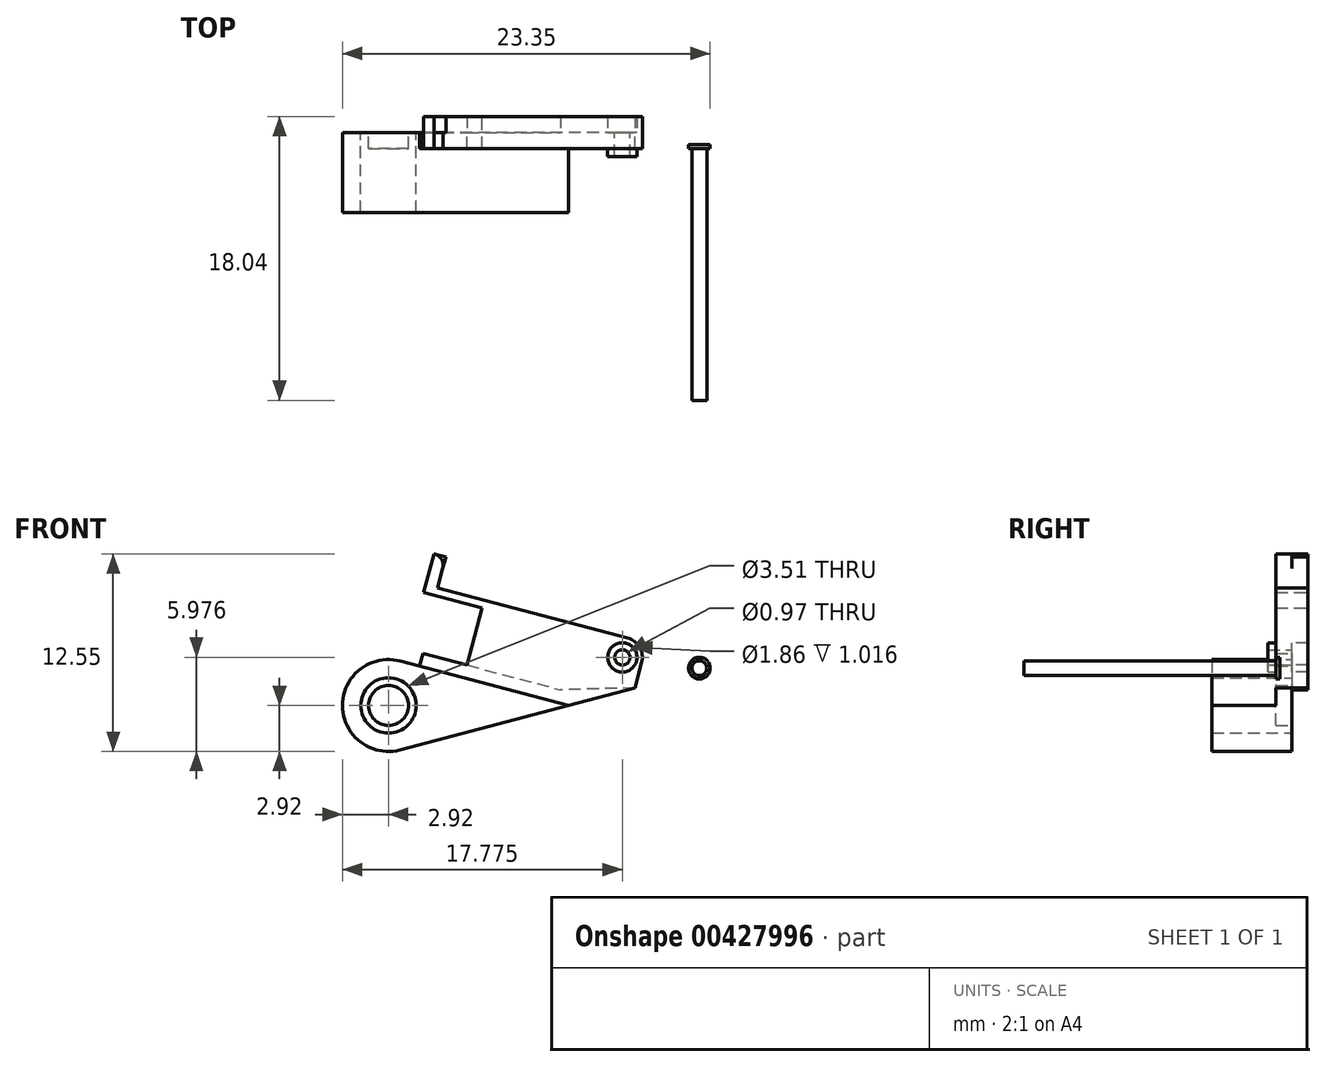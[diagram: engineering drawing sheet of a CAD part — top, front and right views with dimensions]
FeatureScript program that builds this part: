
annotation { "Feature Type Name" : "Feature", "Feature Type Description" : "" }
export const myFeature = defineFeature(function(context is Context, id is Id, definition is map)
    precondition{}
    {
        {
            var Q0;
            Q0=qCreatedBy(makeId("Front.planeOp"),FACE);
            var sketch = newSketch(context, id + "F0", { "sketchPlane" : qUnion([Q0])});
            skCircle(sketch, "E0", {"center": v(0, 0) * mm, "radius": 1.27 * mm});
            skCircle(sketch, "E1", {"center": v(0, 0) * mm, "radius": 2.92 * mm});
            skLineSegment(sketch, "E2", {"start": v(0.75, 2.82) * mm, "end": v(11.43, 0) * mm});
            skLineSegment(sketch, "E3", {"start": v(11.43, 0) * mm, "end": v(0.75, -2.82) * mm});
            skCircle(sketch, "E4", {"center": v(0, 0) * mm, "radius": 1.76 * mm});
            skLineSegment(sketch, "E5", {"start": v(1.97, 2.5) * mm, "end": v(2.19, 3.3) * mm});
            skLineSegment(sketch, "E6", {"start": v(2.19, 3.3) * mm, "end": v(4.98, 2.56) * mm});
            skLineSegment(sketch, "E7", {"start": v(4.98, 2.56) * mm, "end": v(5.94, 6.19) * mm});
            skLineSegment(sketch, "E8", {"start": v(5.94, 6.19) * mm, "end": v(2.24, 7.17) * mm});
            skLineSegment(sketch, "E9", {"start": v(2.24, 7.17) * mm, "end": v(2.89, 9.63) * mm});
            skLineSegment(sketch, "E10", {"start": v(2.89, 9.63) * mm, "end": v(3.64, 9.43) * mm});
            skLineSegment(sketch, "E11", {"start": v(3.64, 9.43) * mm, "end": v(3.13, 7.47) * mm});
            skLineSegment(sketch, "E12", {"start": v(3.13, 7.47) * mm, "end": v(9.67, 5.74) * mm});
            skLineSegment(sketch, "E13", {"start": v(9.67, 5.74) * mm, "end": v(15.18, 4.28) * mm});
            skLineSegment(sketch, "E14", {"start": v(16.08, 2.73) * mm, "end": v(15.66, 1.12) * mm});
            skLineSegment(sketch, "E15", {"start": v(15.66, 1.12) * mm, "end": v(11.43, 0) * mm});
            skPoint(sketch, "E16.visualSharp", {"position": v(16.4, 3.96) * mm});
            skArc(sketch, "E16.filletArc", {"start": v(16.08, 2.73) * mm, "mid": v(15.95, 3.7) * mm, "end": v(15.18, 4.28) * mm});
            skLineSegment(sketch, "E17", {"start": v(4.98, 2.56) * mm, "end": v(13.05, 0.43) * mm});
            skCircle(sketch, "E18", {"center": v(14.86, 3.06) * mm, "radius": 0.49 * mm});
            skCircle(sketch, "E19", {"center": v(14.86, 3.06) * mm, "radius": 0.93 * mm});
            skSolve(sketch);
        }
        {
            var Q0;
            Q0=makeQuery(id+"F0.imprint","IMPRINT",FACE,{"disambiguationData":[TD([[makeQuery(id+"F0.imprint","IMPRINT",EDGE,{"derivedFrom":sQuery(id+"F0.wireOp",EDGE,"E0")}),1.0]])]});
            var Q1;
            {var subQ0=sQuery(id+"F0.wireOp",EDGE,"E2");Q1=makeQuery(id+"F0.imprint","IMPRINT",FACE,{"disambiguationData":[TD([[makeQuery(id+"F0.imprint","IMPRINT",EDGE,{"derivedFrom":subQ0}),-1.0]])]});}
            var Q2;
            Q2=makeQuery(id+"F0.imprint","IMPRINT",FACE,{"disambiguationData":[TD([[makeQuery(id+"F0.imprint","IMPRINT",EDGE,{"derivedFrom":sQuery(id+"F0.wireOp",EDGE,"E4")}),-1.0]])]});
            extrude(context, id + "F1", {"entities" : qUnion([Q0, Q1, Q2]), "depth" : 5.08 * mm});
        }
        {
            var Q0;
            Q0=makeQuery(id+"F1.opExtrude","CAP_FACE",FACE,{"disambiguationData":[OSD([sQuery(id+"F0.wireOp",EDGE,"E0"),sQuery(id+"F0.wireOp",EDGE,"E1"),sQuery(id+"F0.wireOp",EDGE,"E2"),sQuery(id+"F0.wireOp",EDGE,"E3")])],"isStart":false});
            var sketch = newSketch(context, id + "F2", { "sketchPlane" : qUnion([Q0])});
            skCircle(sketch, "E20.0", {"center": v(0, 0) * mm, "radius": 1.76 * mm});
            skSolve(sketch);
        }
        {
            var Q0;
            Q0=makeQuery(id+"F2.imprint","IMPRINT",FACE,{"disambiguationData":[TD([[makeQuery(id+"F2.imprint","IMPRINT",EDGE,{"derivedFrom":sQuery(id+"F2.wireOp",EDGE,"E20.0")}),1.0]])]});
            extrude(context, id + "F3", {"entities" : qUnion([Q0]), "operationType" : NewBodyOperationType.REMOVE, "oppositeDirection" : true, "depth" : 4.06 * mm});
        }
        {
            var Q0;
            {var subQ4=sQuery(id+"F0.wireOp",EDGE,"E5");Q0=makeQuery(id+"F0.imprint","IMPRINT",FACE,{"disambiguationData":[TD([[makeQuery(id+"F0.imprint","IMPRINT",EDGE,{"derivedFrom":subQ4}),-1.0]])]});}
            extrude(context, id + "F4", {"entities" : qUnion([Q0]), "operationType" : NewBodyOperationType.ADD, "depth" : 1.02 * mm});
        }
        {
            var Q0;
            Q0=makeQuery(id+"F0.imprint","IMPRINT",FACE,{"disambiguationData":[TD([[makeQuery(id+"F0.imprint","IMPRINT",EDGE,{"derivedFrom":sQuery(id+"F0.wireOp",EDGE,"E7")}),-1.0]])]});
            var Q1;
            Q1=makeQuery(id+"F0.imprint","IMPRINT",FACE,{"disambiguationData":[TD([[makeQuery(id+"F0.imprint","IMPRINT",EDGE,{"derivedFrom":sQuery(id+"F0.wireOp",EDGE,"E18")}),-1.0]])]});
            extrude(context, id + "F5", {"entities" : qUnion([Q0, Q1]), "operationType" : NewBodyOperationType.ADD, "depth" : 1.02 * mm});
        }
        {
            var Q0;
            Q0=makeQuery(id+"F5.opExtrude","SWEPT_EDGE",EDGE,{"disambiguationData":[OSD([sQuery(id+"F0.wireOp",EDGE,"E10"),sQuery(id+"F0.wireOp",EDGE,"E11")])]});
            fillet(context, id + "F6", {"entities" : qUnion([Q0]), "radius" : 0.76 * mm, "tangentPropagation" : true, "allowEdgeOverflow" : false});
        }
        {
            var Q0;
            {var subQ0=sQuery(id+"F0.wireOp",EDGE,"E17");var subQ1=sQuery(id+"F0.wireOp",EDGE,"E15");Q0=makeQuery(id+"F5.boolean.opBoolean","MERGE",FACE,{"derivedFrom":[makeQuery(id+"F4.opExtrude","CAP_FACE",FACE,{"disambiguationData":[OSD([sQuery(id+"F0.wireOp",EDGE,"E2"),sQuery(id+"F0.wireOp",EDGE,"E5"),sQuery(id+"F0.wireOp",EDGE,"E6"),subQ1,subQ0])],"isStart":false}),makeQuery(id+"F5.opExtrude","CAP_FACE",FACE,{"disambiguationData":[OSD([sQuery(id+"F0.wireOp",EDGE,"E7"),sQuery(id+"F0.wireOp",EDGE,"E8"),sQuery(id+"F0.wireOp",EDGE,"E9"),sQuery(id+"F0.wireOp",EDGE,"E10"),sQuery(id+"F0.wireOp",EDGE,"E11"),sQuery(id+"F0.wireOp",EDGE,"E12"),sQuery(id+"F0.wireOp",EDGE,"E13"),sQuery(id+"F0.wireOp",EDGE,"E14"),subQ1,sQuery(id+"F0.wireOp",EDGE,"E16.filletArc"),subQ0,sQuery(id+"F0.wireOp",EDGE,"E18")])],"isStart":false})]});}
            var sketch = newSketch(context, id + "F7", { "sketchPlane" : qUnion([Q0])});
            skCircle(sketch, "E21.0", {"center": v(14.86, 3.06) * mm, "radius": 0.93 * mm});
            skSolve(sketch);
        }
        {
            var Q0;
            Q0=makeQuery(id+"F7.imprint","IMPRINT",FACE,{"disambiguationData":[TD([[makeQuery(id+"F7.imprint","IMPRINT",EDGE,{"derivedFrom":sQuery(id+"F7.wireOp",EDGE,"E21.0")}),1.0]])]});
            extrude(context, id + "F8", {"entities" : qUnion([Q0]), "operationType" : NewBodyOperationType.ADD, "depth" : 0.5 * mm});
        }
        {
            var Q0;
            Q0=makeQuery(id+"F0.imprint","IMPRINT",FACE,{"disambiguationData":[TD([[makeQuery(id+"F0.imprint","IMPRINT",EDGE,{"derivedFrom":sQuery(id+"F0.wireOp",EDGE,"E7")}),-1.0]])]});
            var sketch = newSketch(context, id + "F9", { "sketchPlane" : qUnion([Q0])});
            skLineSegment(sketch, "E22.0.0", {"start": v(11.43, 0) * mm, "end": v(13.05, 0.43) * mm});
            skLineSegment(sketch, "E22.0.1", {"start": v(13.05, 0.43) * mm, "end": v(4.98, 2.56) * mm});
            skLineSegment(sketch, "E22.0.2", {"start": v(4.98, 2.56) * mm, "end": v(2.19, 3.3) * mm});
            skLineSegment(sketch, "E22.0.3", {"start": v(2.19, 3.3) * mm, "end": v(1.97, 2.5) * mm});
            skLineSegment(sketch, "E22.0.4", {"start": v(1.97, 2.5) * mm, "end": v(11.43, 0) * mm});
            skLineSegment(sketch, "E23.0.0", {"start": v(5.94, 6.19) * mm, "end": v(4.98, 2.56) * mm});
            skLineSegment(sketch, "E23.0.1", {"start": v(4.98, 2.56) * mm, "end": v(13.05, 0.43) * mm});
            skLineSegment(sketch, "E23.0.2", {"start": v(13.05, 0.43) * mm, "end": v(15.66, 1.12) * mm});
            skLineSegment(sketch, "E23.0.3", {"start": v(15.66, 1.12) * mm, "end": v(16.08, 2.73) * mm});
            skArc(sketch, "E23.0.4", {"start": v(16.08, 2.73) * mm, "mid": v(15.95, 3.7) * mm, "end": v(15.18, 4.28) * mm});
            skLineSegment(sketch, "E23.0.5", {"start": v(15.18, 4.28) * mm, "end": v(9.67, 5.74) * mm});
            skLineSegment(sketch, "E23.0.6", {"start": v(9.67, 5.74) * mm, "end": v(3.13, 7.47) * mm});
            skLineSegment(sketch, "E23.0.7", {"start": v(3.13, 7.47) * mm, "end": v(3.64, 9.43) * mm});
            skLineSegment(sketch, "E23.0.8", {"start": v(3.64, 9.43) * mm, "end": v(2.89, 9.63) * mm});
            skLineSegment(sketch, "E23.0.9", {"start": v(2.89, 9.63) * mm, "end": v(2.24, 7.17) * mm});
            skLineSegment(sketch, "E23.0.10", {"start": v(2.24, 7.17) * mm, "end": v(5.94, 6.19) * mm});
            skLineSegment(sketch, "E24", {"start": v(15.66, 1.12) * mm, "end": v(7.96, 0.92) * mm});
            skSolve(sketch);
        }
        {
            var Q0;
            {var subQ0=sQuery(id+"F9.wireOp",EDGE,"E23.0.0");Q0=makeQuery(id+"F9.imprint","IMPRINT",FACE,{"disambiguationData":[TD([[makeQuery(id+"F9.imprint","IMPRINT",EDGE,{"derivedFrom":subQ0}),-1.0]])]});}
            extrude(context, id + "F10", {"entities" : qUnion([Q0]), "operationType" : NewBodyOperationType.ADD, "oppositeDirection" : true, "depth" : 1.02 * mm});
        }
        {
            var Q0;
            Q0=makeQuery(id+"F7.imprint","IMPRINT",FACE,{"disambiguationData":[TD([[makeQuery(id+"F7.imprint","IMPRINT",EDGE,{"derivedFrom":makeQuery(id+"F5.opExtrude","CAP_EDGE",EDGE,{"disambiguationData":[OSD([sQuery(id+"F0.wireOp",EDGE,"E18")])],"isStart":false})}),1.0]])]});
            var sketch = newSketch(context, id + "F11", { "sketchPlane" : qUnion([Q0])});
            skCircle(sketch, "E25.0", {"center": v(14.86, 3.06) * mm, "radius": 0.49 * mm});
            skCircle(sketch, "E26", {"center": v(19.75, 2.37) * mm, "radius": 0.47 * mm});
            skCircle(sketch, "E27", {"center": v(19.75, 2.37) * mm, "radius": 0.69 * mm});
            skSolve(sketch);
        }
        {
            var Q0;
            Q0=makeQuery(id+"F11.imprint","IMPRINT",FACE,{"disambiguationData":[TD([[makeQuery(id+"F11.imprint","IMPRINT",EDGE,{"derivedFrom":sQuery(id+"F11.wireOp",EDGE,"E26")}),1.0]])]});
            extrude(context, id + "F12", {"entities" : qUnion([Q0]), "depth" : 16 * mm});
        }
        {
            var Q0;
            Q0=makeQuery(id+"F11.imprint","IMPRINT",FACE,{"disambiguationData":[TD([[makeQuery(id+"F11.imprint","IMPRINT",EDGE,{"derivedFrom":sQuery(id+"F11.wireOp",EDGE,"E26")}),-1.0]])]});
            var Q1;
            Q1=makeQuery(id+"F11.imprint","IMPRINT",FACE,{"disambiguationData":[TD([[makeQuery(id+"F11.imprint","IMPRINT",EDGE,{"derivedFrom":sQuery(id+"F11.wireOp",EDGE,"E26")}),1.0]])]});
            extrude(context, id + "F13", {"entities" : qUnion([Q0, Q1]), "operationType" : NewBodyOperationType.ADD, "oppositeDirection" : true, "depth" : 0.25 * mm});
        }
    });
